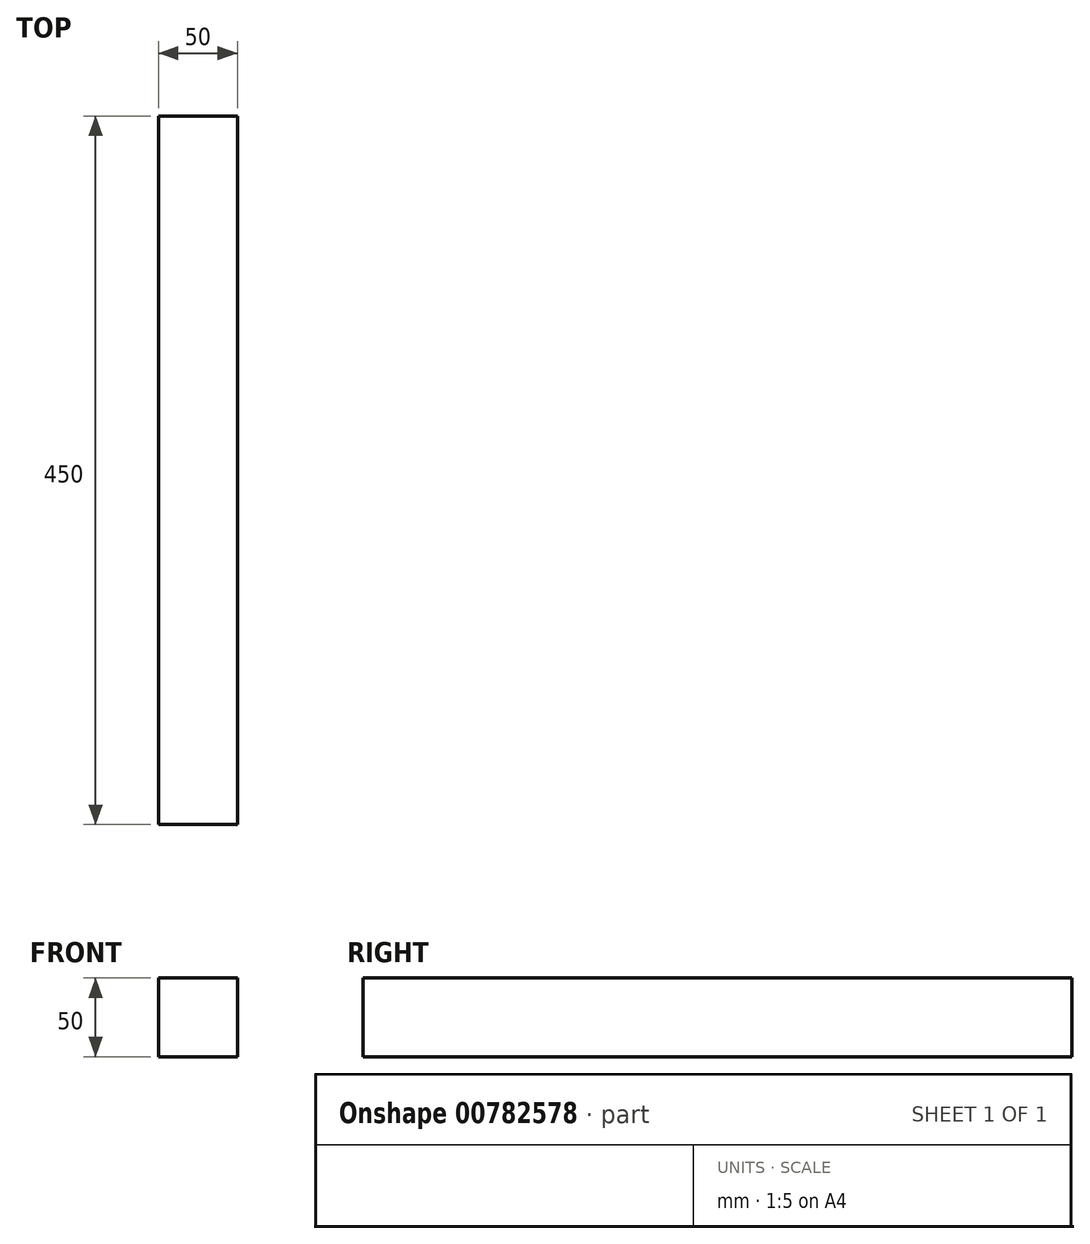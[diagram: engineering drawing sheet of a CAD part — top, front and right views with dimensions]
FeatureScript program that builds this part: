
annotation { "Feature Type Name" : "Feature", "Feature Type Description" : "" }
export const myFeature = defineFeature(function(context is Context, id is Id, definition is map)
    precondition{}
    {
        {
            var Q0;
            Q0=qCreatedBy(makeId("Front.planeOp"),FACE);
            var sketch = newSketch(context, id + "F0", { "sketchPlane" : qUnion([Q0])});
            skLineSegment(sketch, "E0.bottom", {"start": v(0, 0) * mm, "end": v(50, 0) * mm});
            skLineSegment(sketch, "E0.top", {"start": v(0, 50) * mm, "end": v(50, 50) * mm});
            skLineSegment(sketch, "E0.left", {"start": v(0, 0) * mm, "end": v(0, 50) * mm});
            skLineSegment(sketch, "E0.right", {"start": v(50, 0) * mm, "end": v(50, 50) * mm});
            skSolve(sketch);
        }
        {
            var Q0;
            Q0 = qSketchRegion(id + "F0", true);
            extrude(context, id + "F1", {"entities" : qUnion([Q0]), "depth" : 450 * mm, "offsetDistance" : 25 * mm});
        }
    });
